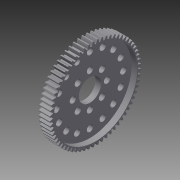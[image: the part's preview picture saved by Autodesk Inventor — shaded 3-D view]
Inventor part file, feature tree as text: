
AUTODESK INVENTOR PART (.ipt)
format: ipt  version: 2015 (Build 190159000, 159)  size: 875,008 bytes
history: native  units: in
note: dims shown in document units (in); Inventor stores cm internally (conversion verified against a paired STEP export)
features: other x3, sketch x2, extrude x2, hole x1
ambient origin geometry x8: Origin, YZ Plane, XZ Plane, XY Plane, X Axis, Y Axis, Z Axis, Center Point
bodies: Solid1 (feature_tree)
feature tree (8):
  other  "User Library-6151941"
  sketch  "Sketch2"  dims[d11=0.5in d13=0.1406in]
  extrude  "Extrusion2"  Depth=0.1406in
  extrude  "Extrusion3"  Depth=0.25in
  hole  "Hole1"  [1 undecoded]
  sketch  "Sketch3"  dims[d14=0.1406in d16=1.0315in d17=1.5748in d19=360.0deg d21=1.5in d22=1.875in d23=3.1496in d25=360.0deg d27=6.2992in d29=360.0deg d31=0.125in d32=0.0in d33=0.4in d34=0.4in d36=0.9605in d37=0.5in d38=1.875in d39=25.1969in d41=360.0deg d43=1.0in d44=0.0in d45=0.14in d46=0.75in d47=0.375in d48=0.25in d49=0.5635in d50=1.0in d51=0.8108in]
  other  "Composite1"
  other  "Srf1"
note: 1 required parameter value undecoded (feature->parameter linkage not recoverable at this tier; creation-order binding heuristic only, values carry confidence <= 0.55)
